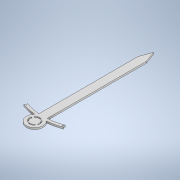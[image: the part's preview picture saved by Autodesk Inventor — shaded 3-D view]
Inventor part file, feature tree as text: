
AUTODESK INVENTOR PART (.ipt)
format: ipt  version: 2022 (Build 260153000, 153)  size: 157,696 bytes
history: native  units: mm
features: other x1, extrude x1, sketch x1
ambient origin geometry x8: Origin, YZ Plane, XZ Plane, XY Plane, X Axis, Y Axis, Z Axis, Center Point
bodies: Body1 (feature_tree)
feature tree (3):
  other  "Твердое тело1"
  extrude  "Выдавливание1"  Depth=59.6mm
  sketch  "Эскиз1"
